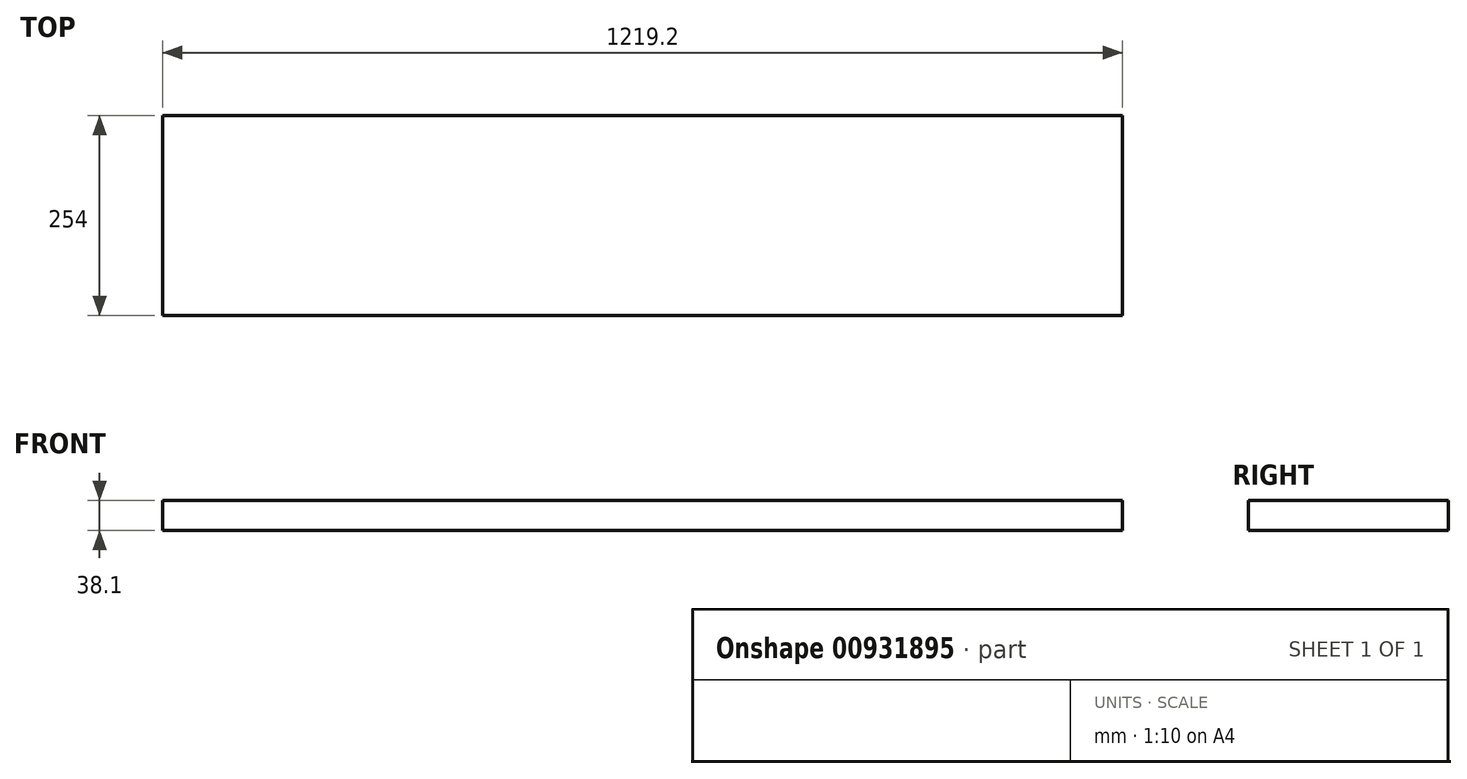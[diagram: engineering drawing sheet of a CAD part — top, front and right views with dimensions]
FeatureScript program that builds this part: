
annotation { "Feature Type Name" : "Feature", "Feature Type Description" : "" }
export const myFeature = defineFeature(function(context is Context, id is Id, definition is map)
    precondition{}
    {
        {
            var Q0;
            Q0=qCreatedBy(makeId("Top.planeOp"),FACE);
            var sketch = newSketch(context, id + "F0", { "sketchPlane" : qUnion([Q0])});
            skLineSegment(sketch, "E0.bottom", {"start": v(0, 0) * mm, "end": v(1219.2, 0) * mm});
            skLineSegment(sketch, "E0.top", {"start": v(0, -254) * mm, "end": v(1219.2, -254) * mm});
            skLineSegment(sketch, "E0.left", {"start": v(0, 0) * mm, "end": v(0, -254) * mm});
            skLineSegment(sketch, "E0.right", {"start": v(1219.2, 0) * mm, "end": v(1219.2, -254) * mm});
            skSolve(sketch);
        }
        {
            var Q0;
            Q0 = qSketchRegion(id + "F0", true);
            extrude(context, id + "F1", {"entities" : qUnion([Q0]), "oppositeDirection" : true, "depth" : 38.1 * mm, "offsetDistance" : 25.4 * mm});
        }
    });
